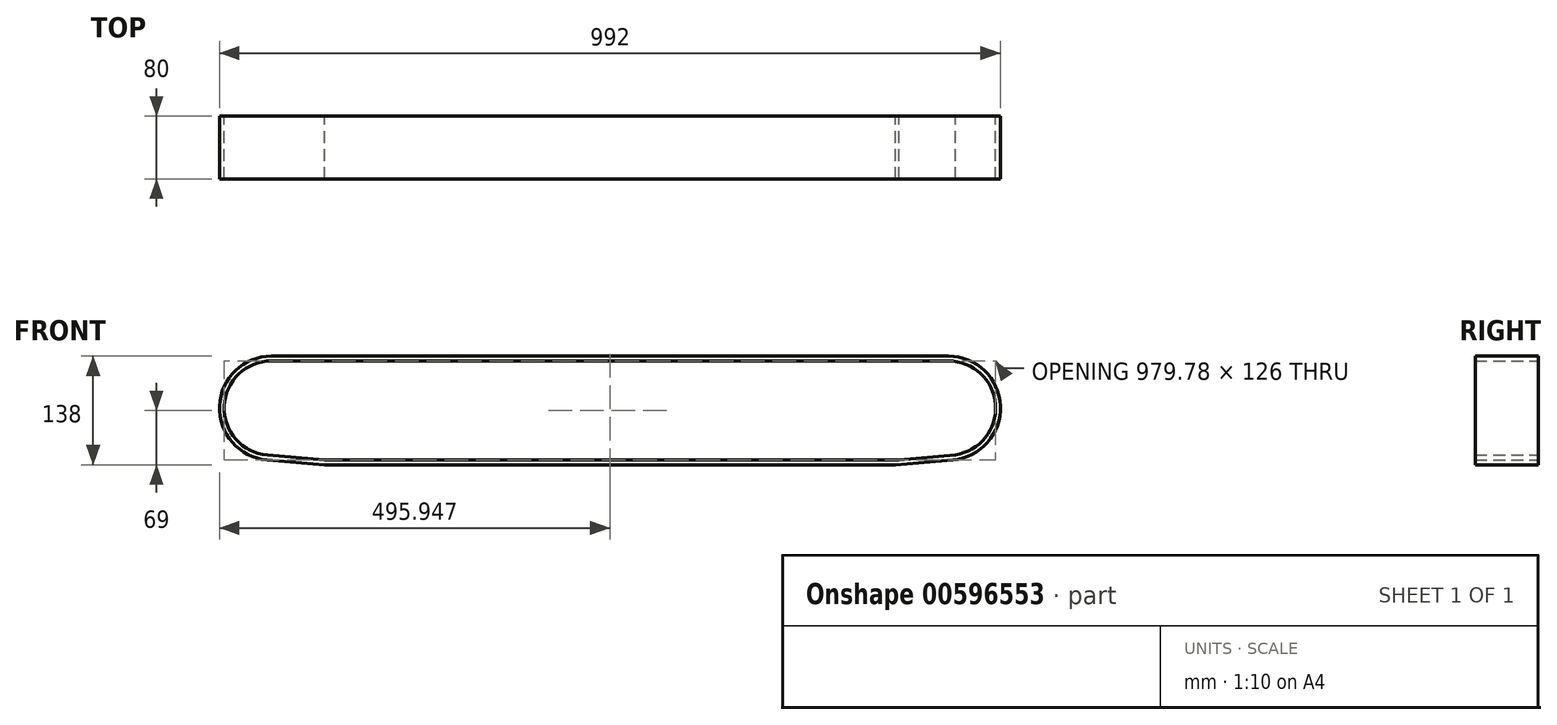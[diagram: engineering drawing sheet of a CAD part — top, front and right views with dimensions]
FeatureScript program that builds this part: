
annotation { "Feature Type Name" : "Feature", "Feature Type Description" : "" }
export const myFeature = defineFeature(function(context is Context, id is Id, definition is map)
    precondition{}
    {
        {
            var Q0;
            Q0=qCreatedBy(makeId("Front.planeOp"),FACE);
            var sketch = newSketch(context, id + "F0", { "sketchPlane" : qUnion([Q0])});
            skArc(sketch, "E0", {"start": v(0, 60) * mm, "mid": v(-59.95, 2.56) * mm, "end": v(-5.12, -59.78) * mm});
            skArc(sketch, "E1", {"start": v(0, 66) * mm, "mid": v(-65.94, 2.8) * mm, "end": v(-5.61, -65.76) * mm});
            skArc(sketch, "E2", {"start": v(865.61, -65.76) * mm, "mid": v(925.94, 2.8) * mm, "end": v(860, 66) * mm});
            skLineSegment(sketch, "E3", {"start": v(0, 66) * mm, "end": v(860, 66) * mm});
            skLineSegment(sketch, "E4", {"start": v(860, 60) * mm, "end": v(0, 60) * mm});
            skLineSegment(sketch, "E5", {"start": v(67.5, -66) * mm, "end": v(797.18, -66) * mm});
            skLineSegment(sketch, "E6", {"start": v(430, 66) * mm, "end": v(430, -66) * mm, "construction": true});
            skLineSegment(sketch, "E7.0", {"start": v(67.5, -72) * mm, "end": v(792.5, -72) * mm});
            skLineSegment(sketch, "E8", {"start": v(67.5, -66) * mm, "end": v(-5.12, -59.78) * mm});
            skLineSegment(sketch, "E9", {"start": v(67.5, -72) * mm, "end": v(-5.61, -65.76) * mm});
            skPoint(sketch, "E10.orphan", {"position": v(0, -66) * mm});
            skLineSegment(sketch, "E11", {"start": v(792.5, -72) * mm, "end": v(865.61, -65.76) * mm});
            skPoint(sketch, "E12.orphan", {"position": v(860, -66) * mm});
            skLineSegment(sketch, "E13", {"start": v(797.18, -66) * mm, "end": v(868.77, -59.36) * mm});
            skArc(sketch, "E14.trimOffspring", {"start": v(868.77, -59.36) * mm, "mid": v(919.84, 4.4) * mm, "end": v(860, 60) * mm});
            skSolve(sketch);
        }
        {
            var Q0;
            Q0 = qSketchRegion(id + "F0", true);
            extrude(context, id + "F1", {"entities" : qUnion([Q0]), "depth" : 80 * mm, "offsetDistance" : 25 * mm});
        }
    });
